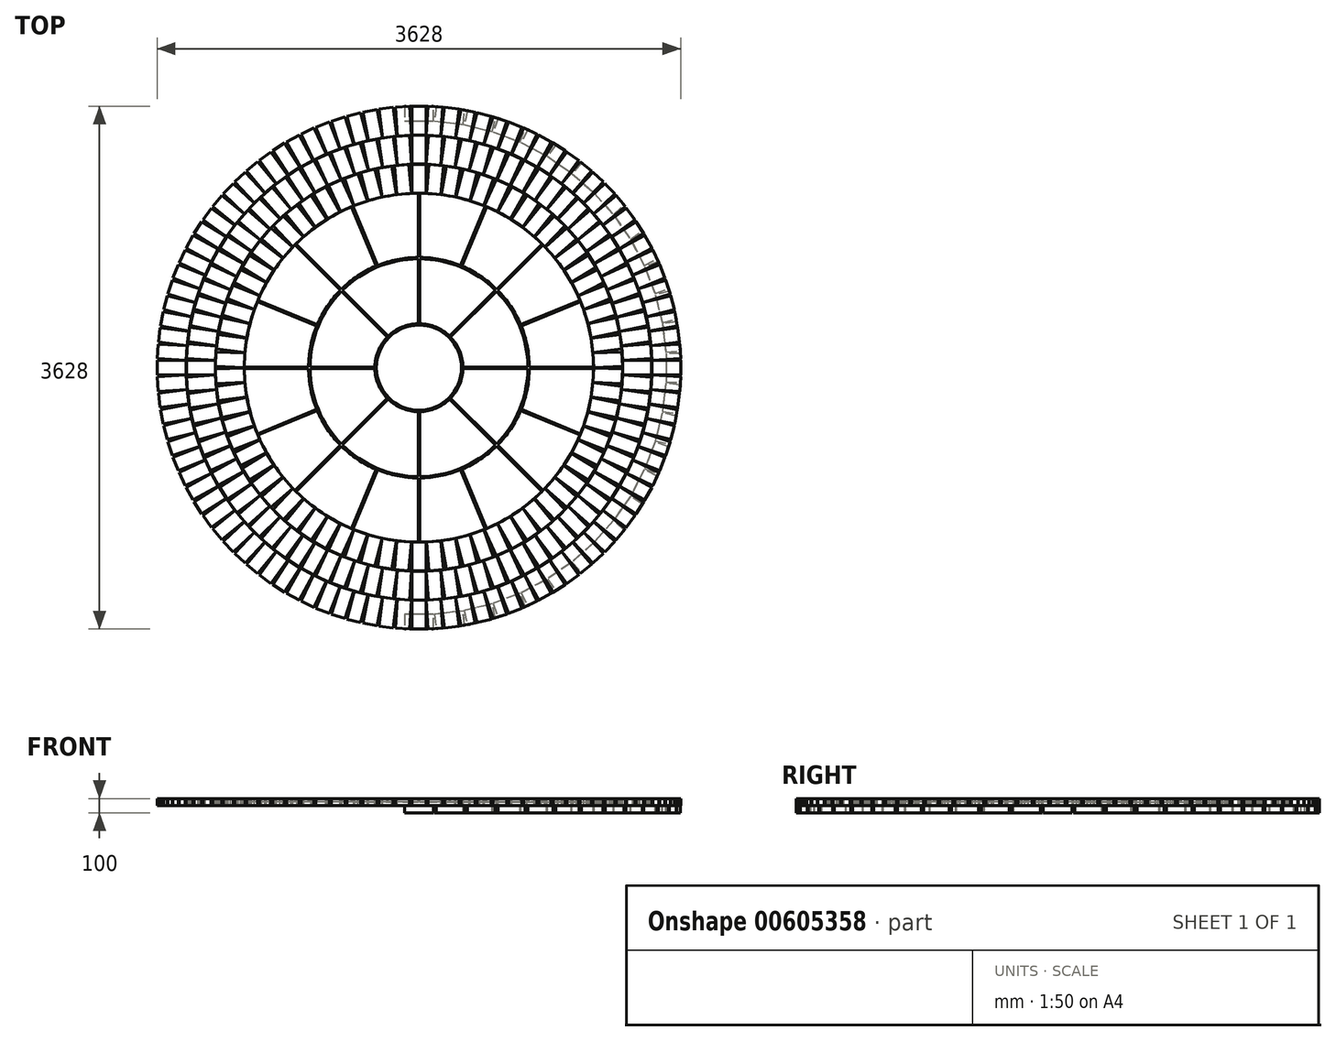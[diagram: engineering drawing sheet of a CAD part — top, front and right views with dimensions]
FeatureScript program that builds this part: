
annotation { "Feature Type Name" : "Feature", "Feature Type Description" : "" }
export const myFeature = defineFeature(function(context is Context, id is Id, definition is map)
    precondition{}
    {
        {
            var Q0;
            Q0=qCreatedBy(makeId("Top.planeOp"),FACE);
            var sketch = newSketch(context, id + "F0", { "sketchPlane" : qUnion([Q0])});
            skCircle(sketch, "E0", {"center": v(0, 0) * mm, "radius": 1210 * mm, "construction": true});
            skLineSegment(sketch, "E1", {"start": v(0, 0) * mm, "end": v(0, 1310) * mm, "construction": true});
            skLineSegment(sketch, "E2", {"start": v(0, 1210) * mm, "end": v(50, 1210) * mm});
            skLineSegment(sketch, "E3", {"start": v(50, 1210) * mm, "end": v(50, 1410) * mm});
            skLineSegment(sketch, "E4", {"start": v(50, 1410) * mm, "end": v(0, 1410) * mm});
            skLineSegment(sketch, "E5.MirrorCS", {"start": v(-50, 1210) * mm, "end": v(-50, 1410) * mm});
            skLineSegment(sketch, "E6.MirrorCS", {"start": v(-50, 1410) * mm, "end": v(0, 1410) * mm});
            skLineSegment(sketch, "E7.MirrorCS", {"start": v(0, 1210) * mm, "end": v(-50, 1210) * mm});
            skPoint(sketch, "E8", {"position": v(-50, 1310) * mm});
            skSolve(sketch);
        }
        {
            var Q0;
            Q0=makeQuery(id+"F0.imprint","IMPRINT",FACE,{"disambiguationData":[TD([[makeQuery(id+"F0.imprint","IMPRINT",EDGE,{"derivedFrom":sQuery(id+"F0.wireOp",EDGE,"E2")}),1.0]])]});
            extrude(context, id + "F1", {"entities" : qUnion([Q0]), "oppositeDirection" : true, "depth" : 50 * mm, "offsetDistance" : 25 * mm});
        }
        {
            var Q0;
            Q0=qCreatedBy(makeId("Front.planeOp"),FACE);
            var sketch = newSketch(context, id + "F2", { "sketchPlane" : qUnion([Q0])});
            skLineSegment(sketch, "E9", {"start": v(0, 0) * mm, "end": v(0, 467.4) * mm});
            skSolve(sketch);
        }
        {
            var Q0;
            Q0=makeQuery(id+"F1.opExtrude","SWEPT_BODY",BODY,{"disambiguationData":[OSD([sQuery(id+"F0.wireOp",EDGE,"E2"),sQuery(id+"F0.wireOp",EDGE,"E3"),sQuery(id+"F0.wireOp",EDGE,"E4"),sQuery(id+"F0.wireOp",EDGE,"E6.MirrorCS"),sQuery(id+"F0.wireOp",EDGE,"E7.MirrorCS"),sQuery(id+"F0.wireOp",EDGE,"E5.MirrorCS")])]});
            var Q1;
            Q1=sQuery(id+"F2.wireOp",EDGE,"E9");
            circularPattern(context, id + "F3", {"entities" : qUnion([Q0]), "axis" : qUnion([Q1]), "angle" : 360 * degree, "instanceCount" : 74, "equalSpace" : true});
        }
        {
            var Q0;
            Q0=qCreatedBy(makeId("Top.planeOp"),FACE);
            var sketch = newSketch(context, id + "F4", { "sketchPlane" : qUnion([Q0])});
            skLineSegment(sketch, "E10", {"start": v(0, 0) * mm, "end": v(0, 1612) * mm, "construction": true});
            skLineSegment(sketch, "E11.bottom", {"start": v(50, 1412) * mm, "end": v(-50, 1412) * mm});
            skLineSegment(sketch, "E11.top", {"start": v(50, 1612) * mm, "end": v(-50, 1612) * mm});
            skLineSegment(sketch, "E11.left", {"start": v(50, 1412) * mm, "end": v(50, 1612) * mm});
            skLineSegment(sketch, "E11.right", {"start": v(-50, 1412) * mm, "end": v(-50, 1612) * mm});
            skPoint(sketch, "E11.middle", {"position": v(0, 1512) * mm});
            skSolve(sketch);
        }
        {
            var Q0;
            Q0=qSketchRegion(id+"F4",true);
            extrude(context, id + "F5", {"entities" : qUnion([Q0]), "oppositeDirection" : true, "depth" : 50 * mm, "offsetDistance" : 25 * mm});
        }
        {
            var Q0;
            Q0=makeQuery(id+"F5.opExtrude","CAP_FACE",FACE,{"disambiguationData":[OSD([sQuery(id+"F4.wireOp",EDGE,"E11.bottom"),sQuery(id+"F4.wireOp",EDGE,"E11.top"),sQuery(id+"F4.wireOp",EDGE,"E11.left"),sQuery(id+"F4.wireOp",EDGE,"E11.right")])],"isStart":true});
            extrude(context, id + "F6", {"entities" : qUnion([Q0]), "operationType" : NewBodyOperationType.ADD, "oppositeDirection" : true, "depth" : 50 * mm, "offsetDistance" : 25 * mm});
        }
        {
            var Q0;
            Q0=makeQuery(id+"F5.opExtrude","SWEPT_BODY",BODY,{"disambiguationData":[OSD([sQuery(id+"F4.wireOp",EDGE,"E11.bottom"),sQuery(id+"F4.wireOp",EDGE,"E11.top"),sQuery(id+"F4.wireOp",EDGE,"E11.left"),sQuery(id+"F4.wireOp",EDGE,"E11.right")])]});
            var Q1;
            Q1=sQuery(id+"F2.wireOp",EDGE,"E9");
            circularPattern(context, id + "F7", {"entities" : qUnion([Q0]), "axis" : qUnion([Q1]), "angle" : 360 * degree, "instanceCount" : 88, "equalSpace" : true});
        }
        {
            var Q0;
            Q0=qCreatedBy(makeId("Top.planeOp"),FACE);
            var sketch = newSketch(context, id + "F8", { "sketchPlane" : qUnion([Q0])});
            skLineSegment(sketch, "E12", {"start": v(0, 0) * mm, "end": v(0, 1714) * mm});
            skLineSegment(sketch, "E13.bottom", {"start": v(-50, 1814) * mm, "end": v(50, 1814) * mm});
            skLineSegment(sketch, "E13.top", {"start": v(-50, 1614) * mm, "end": v(50, 1614) * mm});
            skLineSegment(sketch, "E13.left", {"start": v(-50, 1814) * mm, "end": v(-50, 1614) * mm});
            skLineSegment(sketch, "E13.right", {"start": v(50, 1814) * mm, "end": v(50, 1614) * mm});
            skPoint(sketch, "E13.middle", {"position": v(0, 1714) * mm});
            skSolve(sketch);
        }
        {
            var Q0;
            Q0=qSketchRegion(id+"F8",true);
            extrude(context, id + "F9", {"entities" : qUnion([Q0]), "oppositeDirection" : true, "depth" : 50 * mm, "offsetDistance" : 25 * mm});
        }
        {
            var Q0;
            Q0=makeQuery(id+"F9.opExtrude","SWEPT_BODY",BODY,{"disambiguationData":[OSD([sQuery(id+"F8.wireOp",EDGE,"E13.bottom"),sQuery(id+"F8.wireOp",EDGE,"E13.top"),sQuery(id+"F8.wireOp",EDGE,"E13.left"),sQuery(id+"F8.wireOp",EDGE,"E13.right")])]});
            var Q1;
            Q1=sQuery(id+"F2.wireOp",EDGE,"E9");
            circularPattern(context, id + "F10", {"entities" : qUnion([Q0]), "axis" : qUnion([Q1]), "angle" : 360 * degree, "instanceCount" : 100, "equalSpace" : true});
        }
        {
            var Q0;
            Q0=qCreatedBy(makeId("Top.planeOp"),FACE);
            var sketch = newSketch(context, id + "F11", { "sketchPlane" : qUnion([Q0])});
            skLineSegment(sketch, "E14", {"start": v(0, 0) * mm, "end": v(475.03, 1146.83) * mm, "construction": true});
            skLineSegment(sketch, "E15", {"start": v(0, 0) * mm, "end": v(0, 1210) * mm, "construction": true});
            skArc(sketch, "E16", {"start": v(458.42, 1119.8) * mm, "mid": v(236.06, 1186.75) * mm, "end": v(5, 1209.99) * mm});
            skLineSegment(sketch, "E17.0", {"start": v(5, 764.98) * mm, "end": v(5, 1210) * mm});
            skLineSegment(sketch, "E17.1", {"start": v(288.13, 708.67) * mm, "end": v(458.42, 1119.8) * mm});
            skArc(sketch, "E18", {"start": v(288.13, 708.67) * mm, "mid": v(149.24, 750.3) * mm, "end": v(5, 764.98) * mm});
            skSolve(sketch);
        }
        {
            var Q0;
            {var subQ0=sQuery(id+"F11.wireOp",EDGE,"E16");Q0=makeQuery(id+"F11.imprint","IMPRINT",FACE,{"disambiguationData":[TD([[makeQuery(id+"F11.imprint","IMPRINT",EDGE,{"derivedFrom":subQ0}),1.0]])]});}
            extrude(context, id + "F12", {"entities" : qUnion([Q0]), "oppositeDirection" : true, "depth" : 25 * mm, "offsetDistance" : 25 * mm});
        }
        {
            var Q0;
            Q0=makeQuery(id+"F12.opExtrude","SWEPT_BODY",BODY,{"disambiguationData":[OSD([sQuery(id+"F11.wireOp",EDGE,"E16"),sQuery(id+"F11.wireOp",EDGE,"E17.0"),sQuery(id+"F11.wireOp",EDGE,"E17.1"),sQuery(id+"F11.wireOp",EDGE,"E18")])]});
            var Q1;
            Q1=sQuery(id+"F2.wireOp",EDGE,"E9");
            circularPattern(context, id + "F13", {"entities" : qUnion([Q0]), "axis" : qUnion([Q1]), "angle" : 360 * degree, "instanceCount" : 16, "equalSpace" : true});
        }
        {
            var Q0;
            Q0=qCreatedBy(makeId("Top.planeOp"),FACE);
            var sketch = newSketch(context, id + "F14", { "sketchPlane" : qUnion([Q0])});
            skLineSegment(sketch, "E19", {"start": v(0, 0) * mm, "end": v(0, 772.46) * mm, "construction": true});
            skLineSegment(sketch, "E20", {"start": v(0, 0) * mm, "end": v(662.55, 662.55) * mm, "construction": true});
            skArc(sketch, "E21", {"start": v(530.32, 537.39) * mm, "mid": v(288.93, 697.53) * mm, "end": v(5, 754.98) * mm});
            skArc(sketch, "E22", {"start": v(212.1, 219.17) * mm, "mid": v(116.72, 281.78) * mm, "end": v(5, 304.96) * mm});
            skLineSegment(sketch, "E23.0", {"start": v(5, 304.96) * mm, "end": v(5, 754.98) * mm});
            skLineSegment(sketch, "E23.1", {"start": v(212.1, 219.17) * mm, "end": v(530.32, 537.39) * mm});
            skSolve(sketch);
        }
        {
            var Q0;
            {var subQ0=sQuery(id+"F14.wireOp",EDGE,"E23.0");Q0=makeQuery(id+"F14.imprint","IMPRINT",FACE,{"disambiguationData":[TD([[makeQuery(id+"F14.imprint","IMPRINT",EDGE,{"derivedFrom":subQ0}),-1.0]])]});}
            extrude(context, id + "F15", {"entities" : qUnion([Q0]), "oppositeDirection" : true, "depth" : 25 * mm, "offsetDistance" : 25 * mm});
        }
        {
            var Q0;
            Q0=makeQuery(id+"F15.opExtrude","SWEPT_BODY",BODY,{"disambiguationData":[OSD([sQuery(id+"F14.wireOp",EDGE,"E21"),sQuery(id+"F14.wireOp",EDGE,"E22"),sQuery(id+"F14.wireOp",EDGE,"E23.0"),sQuery(id+"F14.wireOp",EDGE,"E23.1")])]});
            var Q1;
            Q1=sQuery(id+"F2.wireOp",EDGE,"E9");
            circularPattern(context, id + "F16", {"entities" : qUnion([Q0]), "axis" : qUnion([Q1]), "angle" : 360 * degree, "instanceCount" : 8, "equalSpace" : true});
        }
        {
            var Q0;
            Q0=qCreatedBy(makeId("Top.planeOp"),FACE);
            var sketch = newSketch(context, id + "F17", { "sketchPlane" : qUnion([Q0])});
            skCircle(sketch, "E24", {"center": v(0, 0) * mm, "radius": 295 * mm});
            skSolve(sketch);
        }
        {
            var Q0;
            Q0 = qSketchRegion(id + "F17", true);
            extrude(context, id + "F18", {"entities" : qUnion([Q0]), "oppositeDirection" : true, "depth" : 25 * mm, "offsetDistance" : 25 * mm});
        }
        {
            var Q0;
            Q0=makeQuery(id+"F9.opExtrude","CAP_FACE",FACE,{"disambiguationData":[OSD([sQuery(id+"F8.wireOp",EDGE,"E13.bottom"),sQuery(id+"F8.wireOp",EDGE,"E13.top"),sQuery(id+"F8.wireOp",EDGE,"E13.left"),sQuery(id+"F8.wireOp",EDGE,"E13.right")])],"isStart":false});
            var sketch = newSketch(context, id + "F19", { "sketchPlane" : qUnion([Q0])});
            skLineSegment(sketch, "E25", {"start": v(0, -1814) * mm, "end": v(0, -1712) * mm, "construction": true});
            skPoint(sketch, "E25.endSnap0", {"position": v(0, -1814) * mm});
            skLineSegment(sketch, "E26", {"start": v(-100, -1812) * mm, "end": v(-100, -1712) * mm});
            skLineSegment(sketch, "E27", {"start": v(-100, -1712) * mm, "end": v(100, -1712) * mm});
            skLineSegment(sketch, "E28", {"start": v(100, -1712) * mm, "end": v(100, -1812) * mm});
            skLineSegment(sketch, "E29", {"start": v(100, -1812) * mm, "end": v(-100, -1812) * mm});
            skPoint(sketch, "E30.orphan", {"position": v(0, -1812) * mm});
            skSolve(sketch);
        }
        {
            var Q0;
            Q0 = qSketchRegion(id + "F19", true);
            extrude(context, id + "F20", {"entities" : qUnion([Q0]), "depth" : 50 * mm, "offsetDistance" : 25 * mm});
        }
        {
            var Q0;
            Q0=makeQuery(id+"F20.opExtrude","SWEPT_BODY",BODY,{"disambiguationData":[OSD([sQuery(id+"F19.wireOp",EDGE,"E26"),sQuery(id+"F19.wireOp",EDGE,"E27"),sQuery(id+"F19.wireOp",EDGE,"E28"),sQuery(id+"F19.wireOp",EDGE,"E29")])]});
            var Q1;
            Q1=sQuery(id+"F2.wireOp",EDGE,"E9");
            circularPattern(context, id + "F21", {"entities" : qUnion([Q0]), "axis" : qUnion([Q1]), "angle" : 180 * degree, "instanceCount" : 27, "oppositeDirection" : true, "equalSpace" : true});
        }
    });
